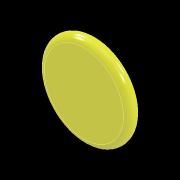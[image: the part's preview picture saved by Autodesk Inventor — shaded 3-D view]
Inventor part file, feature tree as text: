
AUTODESK INVENTOR PART (.ipt)
format: ipt  version: 2020 (Build 240168000, 168)  size: 104,960 bytes
history: native  units: mm
features: other x1, extrude x1, fillet x1, plane x1, sketch x1
ambient origin geometry x8: Origin, YZ Plane, XZ Plane, XY Plane, X Axis, Y Axis, Z Axis, Center Point
bodies: Body1 (feature_tree)
feature tree (5):
  other  "實體1"
  extrude  "擠出1"  Depth=30.0mm
  fillet  "圓角1"  Radius=4.0mm
  plane  "工作平面1"
  sketch  "草圖1"
